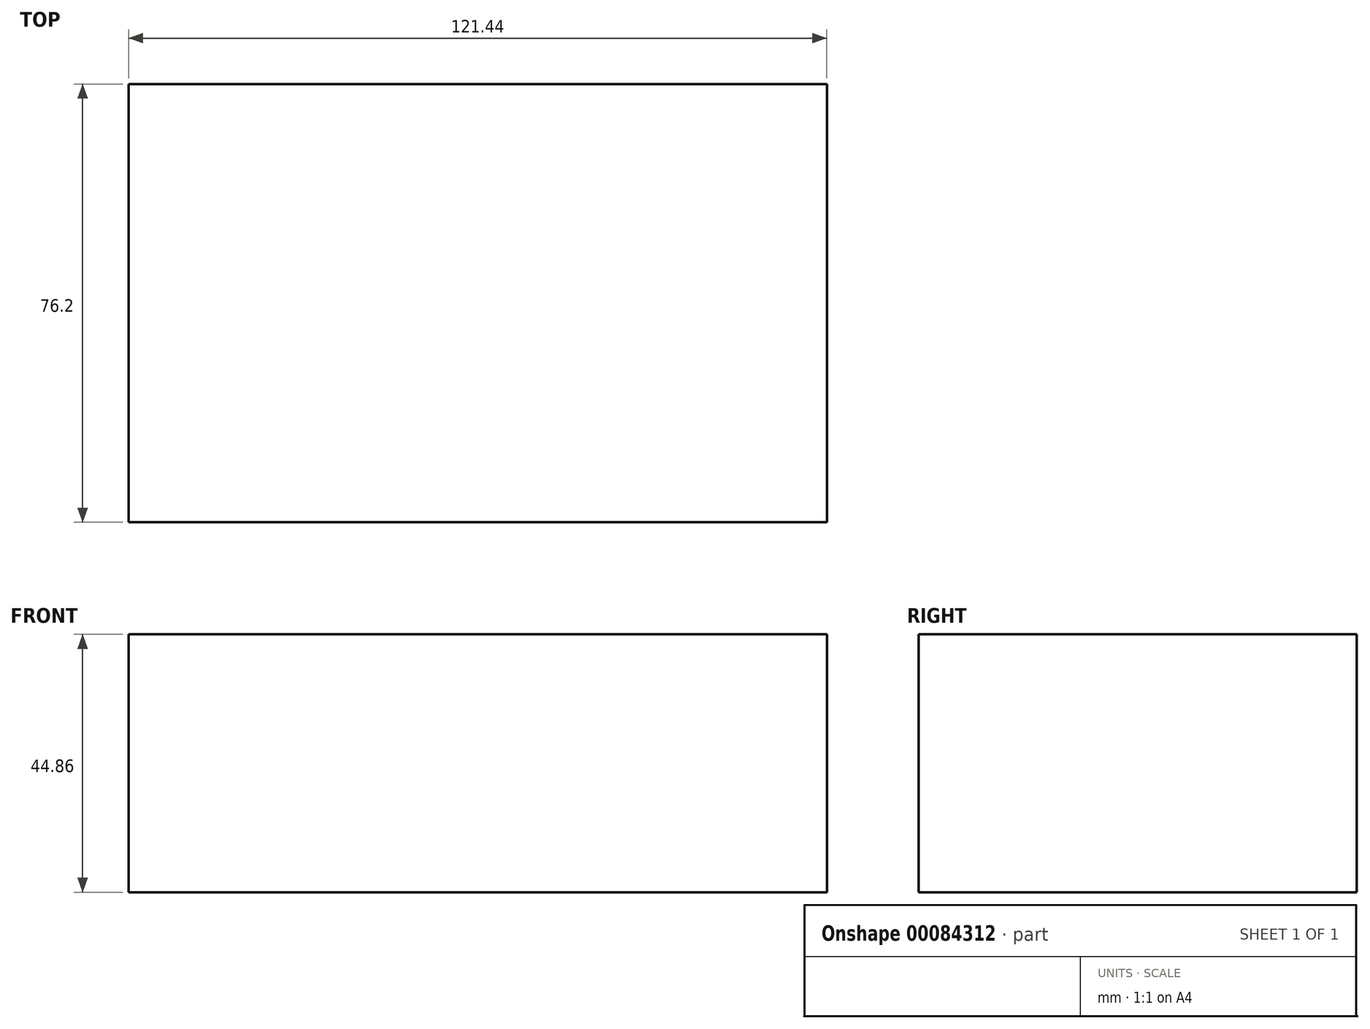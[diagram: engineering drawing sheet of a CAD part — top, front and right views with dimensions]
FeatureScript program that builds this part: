
annotation { "Feature Type Name" : "Feature", "Feature Type Description" : "" }
export const myFeature = defineFeature(function(context is Context, id is Id, definition is map)
    precondition{}
    {
        {
            var Q0;
            Q0=qCreatedBy(makeId("Front.planeOp"),FACE);
            var sketch = newSketch(context, id + "F0", { "sketchPlane" : qUnion([Q0])});
            skLineSegment(sketch, "E0.bottom", {"start": v(-60.72, 22.43) * mm, "end": v(60.72, 22.43) * mm});
            skLineSegment(sketch, "E0.top", {"start": v(-60.72, -22.43) * mm, "end": v(60.72, -22.43) * mm});
            skLineSegment(sketch, "E0.left", {"start": v(-60.72, 22.43) * mm, "end": v(-60.72, -22.43) * mm});
            skLineSegment(sketch, "E0.right", {"start": v(60.72, 22.43) * mm, "end": v(60.72, -22.43) * mm});
            skPoint(sketch, "E0.middle", {"position": v(0, 0) * mm});
            skSolve(sketch);
        }
        {
            var Q0;
            Q0=makeQuery(id+"F0.imprint","IMPRINT",FACE,{"disambiguationData":[TD([[makeQuery(id+"F0.imprint","IMPRINT",EDGE,{"derivedFrom":sQuery(id+"F0.wireOp",EDGE,"E0.bottom")}),-1.0]])]});
            extrude(context, id + "F1", {"entities" : qUnion([Q0]), "endBound" : BoundingType.SYMMETRIC, "depth" : 76.2 * mm});
        }
    });
